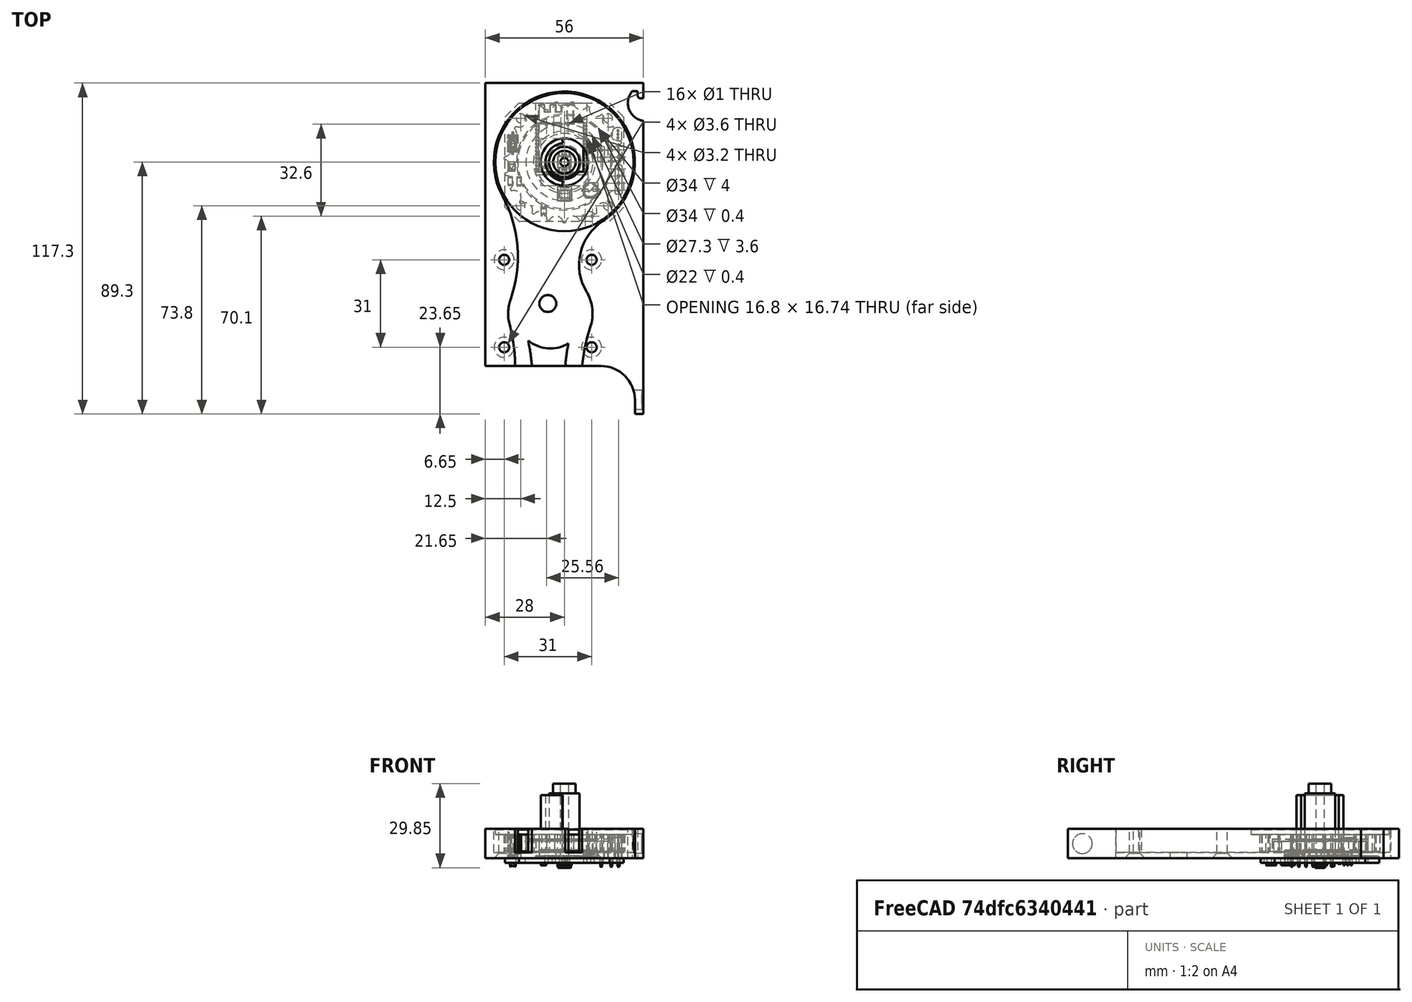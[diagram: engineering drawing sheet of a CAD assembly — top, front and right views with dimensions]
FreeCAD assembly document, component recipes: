
FREECAD ASSEMBLY — COMPONENT RECIPES ("integrated-roller-clutch-v2")

This assembly document has 6 components, labeled P0..P5 below (a component is one placed body or linked part). 5 of them carry a construction recipe — the FreeCAD feature program that regenerates the part from scratch, quoted from this document or its linked companion documents; the rest are supplied as boundary geometry only. No exploded tour is included for this assembly.
COMPONENT P0 — geometry summary ("driver-board"; no construction recipe available for this part):
  bounding box: 42.0 x 42.0 x 11.9 mm
  tessellated surface: 43,692 triangles
  volume: 4223 mm^3 (20% of its bounding box)
COMPONENT P1 — recipe-attached ("Bracket", modeled in this document).
Construction recipe (the document's own serialized feature program — sketch geometry with constraints, then the solid features built on it; lengths are millimeters unless a unit is written):

FEATURE [Sketcher::SketchObject] Sketch
  FullyConstrained = true
  MapMode = 5
  Support = -> [XY_Plane]
  expr: Constraints[10] = 50
  sketch-geometry (18):
    g0: Circle CenterX=0 CenterY=0 CenterZ=0 NormalX=0 NormalY=0 NormalZ=1 AngleXU=0 Radius=25
    g1: LineSegment StartX=-28 StartY=28 StartZ=0 EndX=28 EndY=28 EndZ=0
    g2: LineSegment StartX=28 StartY=28 StartZ=0 EndX=28 EndY=-89.3 EndZ=0
    g3: LineSegment StartX=28 StartY=-89.3 StartZ=0 EndX=25 EndY=-89.3 EndZ=0
    g4: LineSegment StartX=25 StartY=-89.3 StartZ=0 EndX=25 EndY=-84.3 EndZ=0
    g5: LineSegment StartX=13 StartY=-72.3 StartZ=0 EndX=-28 EndY=-72.3 EndZ=0
    g6: LineSegment StartX=-28 StartY=-72.3 StartZ=0 EndX=-28 EndY=28 EndZ=0
    g7: ArcOfCircle CenterX=13 CenterY=-84.3 CenterZ=0 NormalX=0 NormalY=0 NormalZ=1 AngleXU=0 Radius=12 StartAngle=0 EndAngle=1.5708
    g8: GeomPoint X=0 Y=-25 Z=0
    g9: GeomPoint X=0 Y=-30 Z=0
    g10: LineSegment StartX=14.3 StartY=-30 StartZ=0 EndX=-26 EndY=-30 EndZ=0
    g11: LineSegment StartX=-26 StartY=-30 StartZ=0 EndX=-26 EndY=-70.3 EndZ=0
    g12: LineSegment StartX=-26 StartY=-70.3 StartZ=0 EndX=14.3 EndY=-70.3 EndZ=0
    g13: LineSegment StartX=14.3 StartY=-70.3 StartZ=0 EndX=14.3 EndY=-30 EndZ=0
    g14: Circle CenterX=-5.85 CenterY=-50.15 CenterZ=0 NormalX=0 NormalY=0 NormalZ=1 AngleXU=0 Radius=28.4964
    g15: Circle CenterX=-5.85 CenterY=-50.15 CenterZ=0 NormalX=0 NormalY=0 NormalZ=1 AngleXU=0 Radius=3
    g16: LineSegment StartX=-28 StartY=-70.3 StartZ=0 EndX=-26 EndY=-70.3 EndZ=0
    g17: LineSegment StartX=-26 StartY=-70.3 StartZ=0 EndX=-26 EndY=-72.3 EndZ=0
  constraints (50):
    c: Coincident(g0,g-1)
    c: Horizontal(g1)
    c: Coincident(g2,g1)
    c: Vertical(g2)
    c: Coincident(g3,g2)
    c: Coincident(g4,g3)
    c: Horizontal(g5)
    c: Vertical(g6)
    c: Vertical(g4)
    c: Horizontal(g3)
    c: Diameter(g0) = 50
    c: Tangent(g7,g4) = -1.5708
    c: Distance(g3) = 3
    c: Tangent(g7,g5) = -1.5708
    c: Distance(g4) = 5
    c: PointOnObject(g8,g0)
    c: PointOnObject(g9,g-2)
    c: Distance(g9,g8) = 5
    c: Diameter(g7) = 24
    c: Coincident(g5,g6)
    c: Coincident(g10,g11)
    c: Coincident(g11,g12)
    c: Coincident(g12,g13)
    c: Coincident(g13,g10)
    c: Equal(g10,g11)
    c: Equal(g10,g12)
    c: Equal(g10,g13)
    c: PointOnObject(g10,g14)
    c: PointOnObject(g11,g14)
    c: PointOnObject(g12,g14)
    c: PointOnObject(g13,g14)
    c: Parallel(g12,g5)
    c: PointOnObject(g9,g10)
    c: Distance(g13) = 40.3
    c: Coincident(g15,g14)
    c: Diameter(g15) = 6
    c: Distance(g10) = 40.3
    c: PointOnObject(g16,g6)
    c: Coincident(g16,g11)
    c: Coincident(g17,g16)
    c: PointOnObject(g17,g5)
    c: Equal(g17,g16)
    c: Distance(g17) = 2
    c: Perpendicular(g12,g17)
    c: Perpendicular(g11,g16)
    c: PointOnObject(g8,g-2)
    c: DistanceY(g-1,g1) = 28
    c: DistanceX(g-1,g1) = 28
    c: Coincident(g1,g6)
    c: Distance(g1) = 56
FEATURE [PartDesign::Pad] Pad
  Direction = (0,0,1)
  Length = 10.4
  Length2 = 100
  Profile = -> Sketch
  Type = 0
  expr: Length = 2 mm + 0.2 mm + Pad001.Length + 0.2 mm + 2 mm
FEATURE [Sketcher::SketchObject] Sketch005
  ExternalGeometry = -> [Pad]
  FullyConstrained = true
  MapMode = 5
  Placement = pos=(0,0,0) rot=(1,0,0;3.14159rad)
  Support = -> [Pad]
  sketch-geometry (9):
    g0: LineSegment StartX=9.65 StartY=34.65 StartZ=0 EndX=9.65 EndY=65.65 EndZ=0
    g1: LineSegment StartX=9.65 StartY=65.65 StartZ=0 EndX=-21.35 EndY=65.65 EndZ=0
    g2: LineSegment StartX=-21.35 StartY=65.65 StartZ=0 EndX=-21.35 EndY=34.65 EndZ=0
    g3: LineSegment StartX=-21.35 StartY=34.65 StartZ=0 EndX=9.65 EndY=34.65 EndZ=0
    g4: Circle CenterX=-5.85 CenterY=50.15 CenterZ=0 NormalX=0 NormalY=0 NormalZ=1 AngleXU=0 Radius=21.9203
    g5: Circle CenterX=-21.35 CenterY=65.65 CenterZ=0 NormalX=0 NormalY=0 NormalZ=1 AngleXU=0 Radius=1.5
    g6: Circle CenterX=9.65 CenterY=65.65 CenterZ=0 NormalX=0 NormalY=0 NormalZ=1 AngleXU=0 Radius=1.5
    g7: Circle CenterX=9.65 CenterY=34.65 CenterZ=0 NormalX=0 NormalY=0 NormalZ=1 AngleXU=0 Radius=1.5
    g8: Circle CenterX=-21.35 CenterY=34.65 CenterZ=0 NormalX=0 NormalY=0 NormalZ=1 AngleXU=0 Radius=1.5
  constraints (22):
    c: Coincident(g0,g1)
    c: Coincident(g1,g2)
    c: Coincident(g2,g3)
    c: Coincident(g3,g0)
    c: Equal(g0,g1)
    c: Equal(g0,g2)
    c: Equal(g0,g3)
    c: PointOnObject(g0,g4)
    c: PointOnObject(g1,g4)
    c: PointOnObject(g2,g4)
    c: PointOnObject(g3,g4)
    c: Coincident(g4,g-4)
    c: Parallel(g1,g-3)
    c: Distance(g3) = 31
    c: Coincident(g5,g1)
    c: Coincident(g6,g0)
    c: Coincident(g7,g0)
    c: Coincident(g8,g2)
    c: Diameter(g8) = 3
    c: Equal(g8,g7)
    c: Equal(g8,g6)
    c: Equal(g8,g5)
FEATURE [PartDesign::Hole] Hole
  BaseFeature = -> Pad
  CustomThreadClearance = 0
  Depth = 25
  DepthType = 0
  Diameter = 3.6
  DrillForDepth = false
  DrillPoint = 1
  DrillPointAngle = 118
  HoleCutCountersinkAngle = 90
  HoleCutCustomValues = false
  HoleCutDepth = 0.5
  HoleCutDiameter = 7.1
  HoleCutType = 2
  ModelThread = false
  Profile = -> Sketch005
  Tapered = false
  TaperedAngle = 90
  ThreadClass = 0
  ThreadDepth = 23.5
  ThreadDepthType = 0
  ThreadDirection = 0
  ThreadFit = 2
  ThreadSize = 9
  ThreadType = 1
  Threaded = false
  UseCustomThreadClearance = false
FEATURE [Sketcher::SketchObject] Sketch006
  ExternalGeometry = -> [Hole]
  FullyConstrained = false
  MapMode = 5
  Placement = pos=(0,0,10.4) rot=(0,0,1;0rad)
  Support = -> [Hole]
  expr: Constraints[22] = 13 * 6 / pi
  expr: Constraints[23] = 13 * 6 / pi + 5.1
  expr: Constraints[7] = 50 mm
  sketch-geometry (13):
    g0: ArcOfCircle CenterX=0 CenterY=0 CenterZ=0 NormalX=0 NormalY=0 NormalZ=1 AngleXU=0 Radius=25 StartAngle=5.28927 EndAngle=9.92129
    g1: ArcOfCircle CenterX=-4.96805 CenterY=-53.6706 CenterZ=0 NormalX=0 NormalY=0 NormalZ=1 AngleXU=0 Radius=14.9641 StartAngle=2.8025 EndAngle=3.40354
    g2: ArcOfCircle CenterX=-4.96805 CenterY=-53.6706 CenterZ=0 NormalX=0 NormalY=0 NormalZ=1 AngleXU=0 Radius=14.9641 StartAngle=5.95611 EndAngle=6.82361
    g3: ArcOfCircle CenterX=-74.4541 CenterY=-72.3 CenterZ=0 NormalX=0 NormalY=0 NormalZ=1 AngleXU=0 Radius=56.9759 StartAngle=0 EndAngle=0.261943
    g4: ArcOfCircle CenterX=64.518 CenterY=-77.2446 CenterZ=0 NormalX=0 NormalY=0 NormalZ=1 AngleXU=0 Radius=58.412 StartAngle=2.81451 EndAngle=3.05684
    g5: ArcOfCircle CenterX=64.518 CenterY=-77.2446 CenterZ=0 NormalX=0 NormalY=0 NormalZ=1 AngleXU=0 Radius=64.3925 StartAngle=2.93924 EndAngle=3.06473
    g6: ArcOfCircle CenterX=-88.5335 CenterY=-79.2912 CenterZ=0 NormalX=0 NormalY=0 NormalZ=1 AngleXU=0 Radius=77.3718 StartAngle=0.0904824 EndAngle=0.208564
    g7: ArcOfCircle CenterX=-4.96805 CenterY=-53.6706 CenterZ=0 NormalX=0 NormalY=0 NormalZ=1 AngleXU=0 Radius=12.4141 StartAngle=4.0257 EndAngle=5.25473
    g8: ArcOfCircle CenterX=-61.9597 CenterY=-33.5686 CenterZ=0 NormalX=0 NormalY=0 NormalZ=1 AngleXU=0 Radius=45.4688 StartAngle=5.94409 EndAngle=6.7797
    g9: ArcOfCircle CenterX=23.7228 CenterY=-36.456 CenterZ=0 NormalX=0 NormalY=0 NormalZ=1 AngleXU=0 Radius=18.4949 StartAngle=2.14768 EndAngle=3.68201
    g10: LineSegment StartX=-17.4782 StartY=-72.3 StartZ=0 EndX=-11.4782 EndY=-72.3 EndZ=0
    g11: LineSegment StartX=0.315673 StartY=-72.3 StartZ=0 EndX=6.31567 EndY=-72.3 EndZ=0
    g12: GeomPoint X=-4.96805 Y=-74.7723 Z=0
  constraints (29):
    c: Coincident(g0,g-1)
    c: Coincident(g2,g1)
    c: Coincident(g5,g4)
    c: Coincident(g7,g1)
    c: Coincident(g7,g6)
    c: Coincident(g7,g5)
    c: Tangent(g9,g0) = 1.5708
    c: Diameter(g0) = 50
    c: Tangent(g0,g8) = 1.5708
    c: Tangent(g8,g1) = 1.5708
    c: Tangent(g2,g9) = 1.5708
    c: Equal(g2,g1)
    c: Tangent(g3,g1) = 1.5708
    c: Tangent(g2,g4) = 1.5708
    c: Coincident(g10,g3)
    c: Coincident(g10,g6)
    c: Coincident(g11,g5)
    c: Coincident(g11,g4)
    c: Equal(g10,g11)
    c: Distance(g10) = 6
    c: Vertical(g12,g1)
    c: Symmetric(g3,g4,g12)
    c: Diameter(g7) = 24.8282
    c: Diameter(g1) = 29.9282
    c: PointOnObject(g6,g-5)
    c: PointOnObject(g3,g-5)
    c: PointOnObject(g5,g-5)
    c: PointOnObject(g4,g-5)
    c: PointOnObject(g3,g-5)
FEATURE [PartDesign::Pocket] Pocket
  BaseFeature = -> Hole
  Direction = (0,0,-1)
  Length = 0
  Length2 = 100
  Offset = -2
  Profile = -> Sketch006
  Type = 3
  UpToFace = -> Hole [Face4]
FEATURE [Sketcher::SketchObject] Sketch007
  FullyConstrained = true
  MapMode = 5
  Placement = pos=(0,0,2) rot=(0,0,1;0rad)
  Support = -> [Pocket]
  expr: Constraints[1] = 33 mm
  expr: Constraints[3] = 22
  sketch-geometry (2):
    g0: Circle CenterX=0 CenterY=0 CenterZ=0 NormalX=0 NormalY=0 NormalZ=1 AngleXU=0 Radius=16.5
    g1: Circle CenterX=0 CenterY=0 CenterZ=0 NormalX=0 NormalY=0 NormalZ=1 AngleXU=0 Radius=11
  constraints (4):
    c: Coincident(g0,g-1)
    c: Diameter(g0) = 33
    c: Coincident(g1,g0)
    c: Diameter(g1) = 22
FEATURE [PartDesign::Pad] Pad002
  BaseFeature = -> Pocket
  Direction = (0,0,1)
  Length = 0.4
  Length2 = 100
  Profile = -> Sketch007
  Type = 0
FEATURE [Sketcher::SketchObject] Sketch020
  FullyConstrained = false
  MapMode = 5
  Placement = pos=(0,0,0) rot=(0.57735,0.57735,0.57735;2.0944rad)
  Support = -> [YZ_Plane]
  sketch-geometry (2):
    g0: Circle CenterX=-84.2293 CenterY=5.2 CenterZ=0 NormalX=0 NormalY=0 NormalZ=1 AngleXU=0 Radius=3.5
    g1: GeomPoint X=-80.7293 Y=5.2 Z=0
  constraints (3):
    c: Diameter(g0) = 7
    c: PointOnObject(g1,g0)
    c: Horizontal(g1,g0)
FEATURE [Sketcher::SketchObject] Sketch019
  FullyConstrained = false
  MapMode = 5
  Placement = pos=(0,0,10.4) rot=(0,0,1;0rad)
  sketch-geometry (7):
    g0: LineSegment StartX=28.0692 StartY=22.5865 StartZ=0 EndX=27.0025 EndY=22.5865 EndZ=0
    g1: LineSegment StartX=26.0025 StartY=23.5865 StartZ=0 EndX=26.0025 EndY=25.0865 EndZ=0
    g2: LineSegment StartX=26.0025 StartY=25.0865 StartZ=0 EndX=24.0025 EndY=25.0865 EndZ=0
    g3: ArcOfCircle CenterX=28.9326 CenterY=20.9584 CenterZ=0 NormalX=0 NormalY=0 NormalZ=1 AngleXU=0 Radius=6.43014 StartAngle=2.4445 EndAngle=4.57772
    g4: LineSegment StartX=28.0692 StartY=14.5865 StartZ=0 EndX=28.0692 EndY=22.5865 EndZ=0
    g5: ArcOfCircle CenterX=27.0025 CenterY=23.5865 CenterZ=0 NormalX=0 NormalY=0 NormalZ=1 AngleXU=0 Radius=1 StartAngle=3.14159 EndAngle=4.71239
    g6: GeomPoint X=22.5025 Y=20.9865 Z=0
  constraints (16):
    c: Horizontal(g0)
    c: Vertical(g1)
    c: Coincident(g2,g1)
    c: Horizontal(g2)
    c: Coincident(g3,g2)
    c: Coincident(g4,g3)
    c: Coincident(g4,g0)
    c: Tangent(g1,g5) = 1.5708
    c: Tangent(g0,g5) = 1.5708
    c: Distance(g4) = 8
    c: DistanceY(g0,g1) = 2.5
    c: PointOnObject(g6,g3)
    c: DistanceY(g6,g2) = 4.1
    c: Radius(g5) = 1
    c: Distance(g2) = 2
    c: DistanceX(g6,g1) = 3.5
FEATURE [Sketcher::SketchObject] Sketch021
  ExternalGeometry = -> [Pad002]
  FullyConstrained = true
  MapMode = 5
  Placement = pos=(0,0,2.4) rot=(0,0,1;0rad)
  Support = -> [Pad002]
  expr: Constraints[1] = 27.3
  sketch-geometry (2):
    g0: Circle CenterX=0 CenterY=0 CenterZ=0 NormalX=0 NormalY=0 NormalZ=1 AngleXU=0 Radius=13.65
    g1: Circle CenterX=0 CenterY=0 CenterZ=0 NormalX=0 NormalY=0 NormalZ=1 AngleXU=0 Radius=16.5
  constraints (4):
    c: Coincident(g0,g-1)
    c: Diameter(g0) = 27.3
    c: Coincident(g1,g0)
    c: Equal(g1,g-3)
FEATURE [PartDesign::Pad] Pad023
  BaseFeature = -> Pad002
  Direction = (0,0,1)
  Length = 3.6
  Length2 = 100
  Profile = -> Sketch021
  Type = 0
FEATURE [Sketcher::SketchObject] Sketch023
  FullyConstrained = true
  MapMode = 5
  Placement = pos=(0,0,2) rot=(0,0,1;0rad)
  Support = -> [Pad023]
  sketch-geometry (1):
    g0: Circle CenterX=0 CenterY=0 CenterZ=0 NormalX=0 NormalY=0 NormalZ=1 AngleXU=0 Radius=6
  constraints (2):
    c: Coincident(g0,g-1)
    c: Diameter(g0) = 12
FEATURE [PartDesign::Pad] Pad024
  BaseFeature = -> Pad023
  Direction = (0,0,1)
  Length = 1
  Length2 = 100
  Profile = -> Sketch023
  Type = 0
FEATURE [Sketcher::SketchObject] Sketch024
  FullyConstrained = true
  MapMode = 5
  Placement = pos=(0,0,3) rot=(0,0,1;0rad)
  Support = -> [Pad024]
  sketch-geometry (1):
    g0: Circle CenterX=0 CenterY=0 CenterZ=0 NormalX=0 NormalY=0 NormalZ=1 AngleXU=0 Radius=5.4
  constraints (2):
    c: Coincident(g0,g-1)
    c: Diameter(g0) = 10.8
FEATURE [PartDesign::Pad] Pad025
  BaseFeature = -> Pad024
  Direction = (0,0,1)
  Length = 20
  Length2 = 100
  Profile = -> Sketch024
  Type = 0
FEATURE [Sketcher::SketchObject] Sketch054
  FullyConstrained = true
  MapMode = 5
  Placement = pos=(0,0,23) rot=(0,0,1;0rad)
  Support = -> [Pad025]
  sketch-geometry (1):
    g0: Circle CenterX=0 CenterY=0 CenterZ=0 NormalX=0 NormalY=0 NormalZ=1 AngleXU=0 Radius=4
  constraints (2):
    c: Coincident(g0,g-1)
    c: Diameter(g0) = 8
FEATURE [PartDesign::Pad] Pad026
  BaseFeature = -> Pad025
  Direction = (0,0,1)
  Length = 3.5
  Length2 = 100
  Profile = -> Sketch054
  Type = 0
FEATURE [PartDesign::Pocket] Pocket007
  BaseFeature = -> Pad026
  Direction = (0,0,-1)
  Length = 5
  Length2 = 100
  Profile = -> Sketch019
  Type = 1
FEATURE [PartDesign::Pocket] Pocket008
  BaseFeature = -> Pocket007
  Direction = (-1,2e-16,-3e-16)
  Length = 0
  Length2 = 100
  Offset = -1.5
  Profile = -> Sketch020
  Type = 3
  UpToFace = -> Pocket007 [Face9]
FEATURE [PartDesign::Hole] Hole001
  BaseFeature = -> Pocket008
  CustomThreadClearance = 0
  Depth = 25
  DepthType = 0
  Diameter = 3.4
  DrillForDepth = false
  DrillPoint = 1
  DrillPointAngle = 118
  HoleCutCountersinkAngle = 90
  HoleCutCustomValues = false
  HoleCutDepth = 0
  HoleCutDiameter = 6.1
  HoleCutType = 0
  ModelThread = false
  Profile = -> Pocket008 [Edge105]
  Tapered = false
  TaperedAngle = 90
  ThreadClass = 0
  ThreadDepth = 23.5
  ThreadDepthType = 0
  ThreadDirection = 0
  ThreadFit = 0
  ThreadSize = 9
  ThreadType = 1
  Threaded = false
  UseCustomThreadClearance = false
FEATURE [PartDesign::Hole] Hole003
  BaseFeature = -> Hole001
  CustomThreadClearance = 0
  Depth = 267.965
  DepthType = 1
  Diameter = 2.9
  DrillForDepth = false
  DrillPoint = 1
  DrillPointAngle = 118
  HoleCutCountersinkAngle = 90
  HoleCutCustomValues = false
  HoleCutDepth = 0
  HoleCutDiameter = 6.1
  HoleCutType = 0
  ModelThread = false
  Profile = -> Pad026 [Face43]
  Tapered = false
  TaperedAngle = 90
  ThreadClass = 0
  ThreadDepth = 267.965
  ThreadDepthType = 0
  ThreadDirection = 0
  ThreadFit = 0
  ThreadSize = 0
  ThreadType = 0
  Threaded = false
  UseCustomThreadClearance = false
FEATURE [PartDesign::Body] Body  label="Bracket"
  Group = -> [Sketch,Pad,Sketch005,Hole,Sketch006,Pocket,Sketch007,Pad002,Pad023,Pad024,Pad025,Pad026,Sketch054,Sketch021,Sketch023,Sketch024,Sketch019,Pocket007,Sketch020,Pocket008,Hole001,Hole003]
  Origin = -> Origin
  Tip = -> Hole003
COMPONENT P2 — recipe-attached ("Stepper Gear", modeled in this document).
Construction recipe (the document's own serialized feature program — sketch geometry with constraints, then the solid features built on it; lengths are millimeters unless a unit is written):

FEATURE [Sketcher::SketchObject] Sketch003
  FullyConstrained = true
  MapMode = 5
  Support = -> [XY_Plane001]
  expr: Constraints[7] = 13 * 6 / pi - 1
  sketch-geometry (3):
    g0: Circle CenterX=0 CenterY=0 CenterZ=0 NormalX=0 NormalY=0 NormalZ=1 AngleXU=0 Radius=11.9141
    g1: ArcOfCircle CenterX=0 CenterY=0 CenterZ=0 NormalX=0 NormalY=0 NormalZ=1 AngleXU=0 Radius=2.575 StartAngle=2.28245 EndAngle=7.14233
    g2: LineSegment StartX=-1.6817 StartY=1.95 StartZ=0 EndX=1.6817 EndY=1.95 EndZ=0
  constraints (8):
    c: Coincident(g0,g-1)
    c: Coincident(g1,g0)
    c: Coincident(g2,g1)
    c: Coincident(g2,g1)
    c: Horizontal(g2)
    c: Diameter(g1) = 5.15
    c: Distance(g0,g2) = 1.95
    c: Diameter(g0) = 23.8282
FEATURE [PartDesign::Pad] Pad001
  Direction = (1,1,1)
  Length = 6
  Length2 = 100
  Profile = -> Sketch003
  Type = 0
FEATURE [Sketcher::SketchObject] Sketch004
  ExternalGeometry = -> [Pad001]
  FullyConstrained = true
  MapMode = 5
  Placement = pos=(0,0,6) rot=(0,0,1;0rad)
  Support = -> [Pad001]
  sketch-geometry (2):
    g0: Circle CenterX=0 CenterY=12.4141 CenterZ=0 NormalX=0 NormalY=0 NormalZ=1 AngleXU=0 Radius=2.55
    g1: GeomPoint X=0 Y=11.9141 Z=0
  constraints (6):
    c: PointOnObject(g0,g-2)
    c: PointOnObject(g1,g-2)
    c: PointOnObject(g1,g-3)
    c: Distance(g0,g1) = 0.5
    c: Diameter(g0) = 5.1
    c: Distance(g-1,g0) = 12.4141
FEATURE [PartDesign::Pocket] Pocket001
  BaseFeature = -> Pad001
  Direction = (1,1,1)
  Length = 5
  Length2 = 100
  Profile = -> Sketch004
  Type = 1
FEATURE [PartDesign::PolarPattern] PolarPattern
  Angle = 360
  Axis = -> Sketch004 [N_Axis]
  BaseFeature = -> Pocket001
  Occurrences = 13
  Originals = -> [Pocket001]
FEATURE [Sketcher::SketchObject] Sketch062
  ExternalGeometry = -> [PolarPattern]
  FullyConstrained = true
  MapMode = 5
  Placement = pos=(0,0,6) rot=(0,0,1;0rad)
  Support = -> [PolarPattern]
  sketch-geometry (1):
    g0: Circle CenterX=0 CenterY=0 CenterZ=0 NormalX=0 NormalY=0 NormalZ=1 AngleXU=0 Radius=2.575
  constraints (2):
    c: Coincident(g0,g-1)
    c: Tangent(g0,g-3)
FEATURE [PartDesign::Pocket] Pocket014
  BaseFeature = -> PolarPattern
  Direction = (1,1,1)
  Length = 1.2
  Length2 = 100
  Profile = -> Sketch062
  Type = 0
FEATURE [PartDesign::Body] Body001  label="Stepper Gear"
  Group = -> [Sketch003,Pad001,Sketch004,Pocket001,PolarPattern,Sketch062,Pocket014]
  Origin = -> Origin001
  Placement = pos=(-5.85,-50.15,2.4) rot=(0,0,1;1.5708rad)
  Tip = -> Pocket014
  expr: .Placement.Base.x = -28 + 2 + 40.3 / 2
  expr: .Placement.Base.y = -(25 + 5 + 40.3 / 2)
  expr: .Placement.Base.z = 2 + 0.4
COMPONENT P3 — recipe-attached ("Cover Gear", modeled in this document).
Construction recipe (the document's own serialized feature program — sketch geometry with constraints, then the solid features built on it; lengths are millimeters unless a unit is written):

FEATURE [Sketcher::SketchObject] Sketch012
  FullyConstrained = true
  MapMode = 5
  Support = -> [XY_Plane002]
  expr: Constraints[1] = 23 * 5.85 / pi
  sketch-geometry (1):
    g0: Circle CenterX=0 CenterY=0 CenterZ=0 NormalX=0 NormalY=0 NormalZ=1 AngleXU=0 Radius=21.4143
  constraints (2):
    c: Coincident(g0,g-1)
    c: Diameter(g0) = 42.8286
FEATURE [PartDesign::Pad] Pad007
  Direction = (1,1,1)
  Length = 6
  Length2 = 100
  Profile = -> Sketch012
  Type = 0
  expr: Length = Pad001.Length
FEATURE [Sketcher::SketchObject] Sketch013
  ExternalGeometry = -> [Pad007]
  FullyConstrained = true
  MapMode = 5
  Placement = pos=(0,0,6) rot=(0,0,1;0rad)
  Support = -> [Pad007]
  sketch-geometry (2):
    g0: Circle CenterX=0 CenterY=21.9143 CenterZ=0 NormalX=0 NormalY=0 NormalZ=1 AngleXU=0 Radius=2.55
    g1: GeomPoint X=0 Y=21.4143 Z=0
  constraints (5):
    c: PointOnObject(g0,g-2)
    c: PointOnObject(g1,g-3)
    c: PointOnObject(g1,g-2)
    c: Distance(g1,g0) = 0.5
    c: Diameter(g0) = 5.1
FEATURE [PartDesign::Pocket] Pocket002
  BaseFeature = -> Pad007
  Direction = (1,1,1)
  Length = 5
  Length2 = 100
  Profile = -> Sketch013
  Type = 1
FEATURE [PartDesign::PolarPattern] PolarPattern001
  Angle = 360
  Axis = -> Sketch013 [N_Axis]
  BaseFeature = -> Pocket002
  Occurrences = 23
  Originals = -> [Pocket002]
FEATURE [Sketcher::SketchObject] Sketch014
  FullyConstrained = true
  MapMode = 5
  Placement = pos=(0,0,0) rot=(1,0,0;3.14159rad)
  Support = -> [PolarPattern001]
  expr: Constraints[1] = 27 + 6 + 1
  expr: Constraints[3] = 20.3
  sketch-geometry (2):
    g0: Circle CenterX=0 CenterY=0 CenterZ=0 NormalX=0 NormalY=0 NormalZ=1 AngleXU=0 Radius=17
    g1: Circle CenterX=0 CenterY=0 CenterZ=0 NormalX=0 NormalY=0 NormalZ=1 AngleXU=0 Radius=10.15
  constraints (4):
    c: Coincident(g0,g-1)
    c: Diameter(g0) = 34
    c: Coincident(g1,g0)
    c: Diameter(g1) = 20.3
FEATURE [PartDesign::Pocket] Pocket003
  BaseFeature = -> PolarPattern001
  Direction = (0,0,1)
  Length = 4
  Length2 = 100
  Profile = -> Sketch014
  Type = 0
FEATURE [Sketcher::SketchObject] Sketch015
  FullyConstrained = true
  MapMode = 5
  Placement = pos=(0,0,0) rot=(1,0,0;3.14159rad)
  Support = -> [Pocket003]
  expr: Constraints[1] = 16.8
  sketch-geometry (1):
    g0: Circle CenterX=0 CenterY=0 CenterZ=0 NormalX=0 NormalY=0 NormalZ=1 AngleXU=0 Radius=8.4
  constraints (2):
    c: Coincident(g0,g-1)
    c: Diameter(g0) = 16.8
FEATURE [PartDesign::Pocket] Pocket004
  BaseFeature = -> Pocket003
  Direction = (0,0,1)
  Length = 5
  Length2 = 100
  Profile = -> Sketch015
  Type = 1
FEATURE [Sketcher::SketchObject] Sketch016
  ExternalGeometry = -> [Pocket004]
  FullyConstrained = true
  MapMode = 5
  Placement = pos=(0,0,0) rot=(1,0,0;3.14159rad)
  Support = -> [Pocket004]
  sketch-geometry (6):
    g0: ArcOfCircle CenterX=0 CenterY=0 CenterZ=0 NormalX=0 NormalY=0 NormalZ=1 AngleXU=0 Radius=8.4 StartAngle=1.65806 EndAngle=4.62512
    g1: ArcOfCircle CenterX=0 CenterY=0 CenterZ=0 NormalX=0 NormalY=0 NormalZ=1 AngleXU=0 Radius=6.7 StartAngle=1.65806 EndAngle=4.62512
    g2: LineSegment StartX=-0.732108 StartY=8.36804 StartZ=0 EndX=-0.583943 EndY=6.6745 EndZ=0
    g3: LineSegment StartX=-0.732108 StartY=-8.36804 StartZ=0 EndX=-0.583943 EndY=-6.6745 EndZ=0
    g4: LineSegment StartX=-0.583943 StartY=-6.6745 StartZ=0 EndX=8.4 EndY=0 EndZ=0
    g5: LineSegment StartX=8.4 StartY=0 StartZ=0 EndX=-0.583943 EndY=6.6745 EndZ=0
  constraints (17):
    c: Coincident(g0,g-1)
    c: PointOnObject(g0,g-3)
    c: Coincident(g1,g0)
    c: Coincident(g2,g0)
    c: Coincident(g2,g1)
    c: Coincident(g3,g0)
    c: Coincident(g3,g1)
    c: Perpendicular(g0,g3)
    c: Perpendicular(g0,g2)
    c: Diameter(g1) = 13.4
    c: Angle(g2,g3) = 2.96706
    c: Coincident(g4,g1)
    c: PointOnObject(g4,g-1)
    c: Coincident(g5,g4)
    c: Coincident(g5,g1)
    c: Equal(g4,g5)
    c: PointOnObject(g4,g-3)
FEATURE [PartDesign::Pad] Pad008
  BaseFeature = -> Pocket004
  Direction = (0,0,-1)
  Length = 20
  Length2 = 100
  Profile = -> Sketch016
  Reversed = true
  Type = 0
FEATURE [Sketcher::SketchObject] Sketch018
  ExternalGeometry = -> [Pad008]
  FullyConstrained = true
  MapMode = 5
  Placement = pos=(0,0,6) rot=(0,0,1;0rad)
  Support = -> [Pad008]
  sketch-geometry (2):
    g0: Circle CenterX=0 CenterY=0 CenterZ=0 NormalX=0 NormalY=0 NormalZ=1 AngleXU=0 Radius=24.5
    g1: Circle CenterX=0 CenterY=0 CenterZ=0 NormalX=0 NormalY=0 NormalZ=1 AngleXU=0 Radius=8.4
  constraints (4):
    c: Coincident(g0,g-1)
    c: Coincident(g1,g0)
    c: PointOnObject(g-3,g1)
    c: Diameter(g0) = 49
FEATURE [PartDesign::Pad] Pad009
  BaseFeature = -> Pad008
  Direction = (0,0,1)
  Length = 1.8
  Length2 = 100
  Profile = -> Sketch018
  Type = 0
FEATURE [Sketcher::SketchObject] Sketch060
  ExternalGeometry = -> [Pad009]
  FullyConstrained = true
  MapMode = 5
  Placement = pos=(0,0,4) rot=(1,0,0;3.14159rad)
  Support = -> [Pad009]
  sketch-geometry (2):
    g0: Circle CenterX=0 CenterY=0 CenterZ=0 NormalX=0 NormalY=0 NormalZ=1 AngleXU=0 Radius=17
    g1: Circle CenterX=0 CenterY=0 CenterZ=0 NormalX=0 NormalY=0 NormalZ=1 AngleXU=0 Radius=11
  constraints (4):
    c: Coincident(g0,g-1)
    c: Equal(g0,g-3)
    c: Coincident(g1,g0)
    c: Diameter(g1) = 22
FEATURE [PartDesign::Pocket] Pocket013
  BaseFeature = -> Pad009
  Direction = (0,0,1)
  Length = 0.4
  Length2 = 100
  Profile = -> Sketch060
  Type = 0
FEATURE [PartDesign::Body] Body002  label="Cover Gear"
  Group = -> [Sketch012,Pad007,Sketch013,Pocket002,PolarPattern001,Sketch014,Pocket003,Sketch015,Pocket004,Sketch016,Pad008,Sketch018,Pad009,Sketch060,Pocket013]
  Origin = -> Origin002
  Placement = pos=(0,0,2.4) rot=(0,0,1;0rad)
  Tip = -> Pocket013
  expr: .Placement.Base.z = 2 + 0.4
COMPONENT P4 — recipe-attached ("Spring", modeled in this document).
Construction recipe (the document's own serialized feature program — sketch geometry with constraints, then the solid features built on it; lengths are millimeters unless a unit is written):

FEATURE [Sketcher::SketchObject] Sketch017
  FullyConstrained = true
  MapMode = 5
  Placement = pos=(0,0,0) rot=(1,0,0;1.5708rad)
  Support = -> [XZ_Plane003]
  expr: Constraints[9] = 10.5 / 2
  sketch-geometry (4):
    g0: LineSegment StartX=5.25 StartY=0 StartZ=0 EndX=6.1 EndY=0 EndZ=0
    g1: LineSegment StartX=6.1 StartY=0 StartZ=0 EndX=6.1 EndY=1.25 EndZ=0
    g2: LineSegment StartX=6.1 StartY=1.25 StartZ=0 EndX=5.25 EndY=1.25 EndZ=0
    g3: LineSegment StartX=5.25 StartY=1.25 StartZ=0 EndX=5.25 EndY=0 EndZ=0
  constraints (12):
    c: Coincident(g0,g1)
    c: Coincident(g1,g2)
    c: Coincident(g2,g3)
    c: Coincident(g3,g0)
    c: Horizontal(g0)
    c: Horizontal(g2)
    c: Vertical(g1)
    c: Vertical(g3)
    c: PointOnObject(g0,g-1)
    c: Distance(g-1,g0) = 5.25
    c: Distance(g1) = 1.25
    c: Distance(g0) = 0.85
FEATURE [PartDesign::AdditiveHelix] AdditiveHelix
  Angle = 0
  Axis = (0,-2e-16,1)
  Base = (0,0,0)
  Growth = 0
  HasBeenEdited = true
  Height = 8.1
  LeftHanded = false
  Mode = 2
  Outside = false
  Pitch = 1.24615
  Placement = pos=(0,0,0) rot=(1,0,0;1.5708rad)
  Profile = -> Sketch017
  ReferenceAxis = -> Sketch017 [V_Axis]
  Turns = 6.5
FEATURE [PartDesign::Body] Body003  label="Spring"
  Group = -> [Sketch017,AdditiveHelix]
  Origin = -> Origin003
  Placement = pos=(0,0,2.2) rot=(0,0,1;0rad)
  Tip = -> AdditiveHelix
COMPONENT P5 — recipe-attached ("Cover Adapter", modeled in this document).
Construction recipe (the document's own serialized feature program — sketch geometry with constraints, then the solid features built on it; lengths are millimeters unless a unit is written):

FEATURE [Sketcher::SketchObject] Sketch049
  FullyConstrained = true
  MapMode = 5
  Support = -> [XY_Plane011]
  sketch-geometry (7):
    g0: ArcOfCircle CenterX=0 CenterY=0 CenterZ=0 NormalX=0 NormalY=0 NormalZ=1 AngleXU=0 Radius=8.1 StartAngle=4.99164 EndAngle=7.57473
    g1: ArcOfCircle CenterX=0 CenterY=0 CenterZ=0 NormalX=0 NormalY=0 NormalZ=1 AngleXU=0 Radius=6.5 StartAngle=4.99164 EndAngle=7.57473
    g2: LineSegment StartX=1.79164 StartY=6.2482 StartZ=0 EndX=2.23266 EndY=7.78622 EndZ=0
    g3: LineSegment StartX=1.79164 StartY=-6.2482 StartZ=0 EndX=2.23266 EndY=-7.78622 EndZ=0
    g4: GeomPoint X=-5 Y=0 Z=0
    g5: LineSegment StartX=-5 StartY=0 StartZ=0 EndX=1.79164 EndY=6.2482 EndZ=0
    g6: LineSegment StartX=-5 StartY=0 StartZ=0 EndX=1.79164 EndY=-6.2482 EndZ=0
  constraints (18):
    c: Coincident(g0,g-1)
    c: Coincident(g1,g0)
    c: Coincident(g2,g1)
    c: Coincident(g2,g0)
    c: Coincident(g3,g1)
    c: Coincident(g3,g0)
    c: Perpendicular(g0,g2)
    c: Perpendicular(g1,g3)
    c: Diameter(g1) = 13
    c: Angle(g3,g2) = 2.58309
    c: PointOnObject(g4,g-1)
    c: Coincident(g5,g4)
    c: Coincident(g5,g1)
    c: Coincident(g6,g4)
    c: Coincident(g6,g1)
    c: Equal(g6,g5)
    c: Distance(g4,g0) = 5
    c: Distance(g2) = 1.6
FEATURE [Sketcher::SketchObject] Sketch050
  FullyConstrained = true
  MapMode = 5
  Placement = pos=(0,0,8.4) rot=(0,0,1;0rad)
  sketch-geometry (1):
    g0: Circle CenterX=0 CenterY=0 CenterZ=0 NormalX=0 NormalY=0 NormalZ=1 AngleXU=0 Radius=12.4
  constraints (2):
    c: Coincident(g0,g-1)
    c: Diameter(g0) = 24.8
FEATURE [PartDesign::Pad] Pad022
  AllowMultiFace = false
  Direction = (1,1,1)
  Length = 20
  Length2 = 100
  Placement = pos=(0,0,8.4) rot=(0,0,1;0rad)
  Profile = -> Sketch050
  Type = 0
  expr: Length = 20
FEATURE [Sketcher::SketchObject] Sketch058
  FullyConstrained = true
  MapMode = 5
  Placement = pos=(0,0,24.1) rot=(1,0,0;3.14159rad)
  sketch-geometry (1):
    g0: Circle CenterX=0 CenterY=0 CenterZ=0 NormalX=0 NormalY=0 NormalZ=1 AngleXU=0 Radius=5.5
  constraints (2):
    c: Coincident(g0,g-1)
    c: Diameter(g0) = 11
FEATURE [PartDesign::Pad] Pad027
  BaseFeature = -> Pad022
  Direction = (1,1,1)
  Length = 10
  Length2 = 100
  Placement = pos=(0,0,8.4) rot=(0,0,1;0rad)
  Profile = -> Sketch049
  Type = 3
  UpToFace = -> Pad022 [Face2]
FEATURE [Sketcher::SketchObject] Sketch056
  ExternalGeometry = -> [Pad027]
  FullyConstrained = true
  MapMode = 5
  Placement = pos=(0,0,8.4) rot=(1,0,0;3.14159rad)
  sketch-geometry (4):
    g0: ArcOfCircle CenterX=0 CenterY=0 CenterZ=0 NormalX=0 NormalY=0 NormalZ=1 AngleXU=0 Radius=9 StartAngle=1.29154 EndAngle=4.99164
    g1: ArcOfCircle CenterX=0 CenterY=0 CenterZ=0 NormalX=0 NormalY=0 NormalZ=1 AngleXU=0 Radius=6.5 StartAngle=4.99164 EndAngle=7.57473
    g2: LineSegment StartX=1.79164 StartY=6.2482 StartZ=0 EndX=2.48074 EndY=8.65136 EndZ=0
    g3: LineSegment StartX=1.79164 StartY=-6.2482 StartZ=0 EndX=2.48074 EndY=-8.65136 EndZ=0
  constraints (11):
    c: Coincident(g0,g-1)
    c: Coincident(g1,g0)
    c: Coincident(g1,g-3)
    c: Coincident(g1,g-3)
    c: Coincident(g2,g1)
    c: Coincident(g3,g1)
    c: Coincident(g0,g2)
    c: Coincident(g0,g3)
    c: PointOnObject(g-4,g2)
    c: PointOnObject(g-4,g3)
    c: Diameter(g0) = 18
FEATURE [PartDesign::Pocket] Pocket009
  BaseFeature = -> Pad027
  Direction = (1,1,1)
  Length = 12.2
  Length2 = 100
  Placement = pos=(0,0,8.4) rot=(0,0,1;0rad)
  Profile = -> Sketch056
  Type = 0
FEATURE [Sketcher::SketchObject] Sketch057
  FullyConstrained = true
  MapMode = 5
  Placement = pos=(0,0,20.6) rot=(1,0,0;3.14159rad)
  Support = -> [Pocket009]
  sketch-geometry (1):
    g0: Circle CenterX=0 CenterY=0 CenterZ=0 NormalX=0 NormalY=0 NormalZ=1 AngleXU=0 Radius=6.05
  constraints (2):
    c: Coincident(g0,g-1)
    c: Diameter(g0) = 12.1
FEATURE [PartDesign::Pocket] Pocket010
  BaseFeature = -> Pocket009
  Direction = (1,1,1)
  Length = 3.5
  Length2 = 100
  Placement = pos=(0,0,8.4) rot=(0,0,1;0rad)
  Profile = -> Sketch057
  Type = 0
FEATURE [PartDesign::Pocket] Pocket011
  BaseFeature = -> Pocket010
  Direction = (1,1,1)
  Length = 5
  Length2 = 100
  Placement = pos=(0,0,8.4) rot=(0,0,1;0rad)
  Profile = -> Sketch058
  Type = 1
FEATURE [Sketcher::SketchObject] Sketch055
  ExternalGeometry = -> [Pocket011]
  FullyConstrained = true
  MapMode = 5
  Placement = pos=(0,0,28.4) rot=(0,0,1;0rad)
  Support = -> [Pocket011]
  sketch-geometry (4):
    g0: ArcOfCircle CenterX=0 CenterY=0 CenterZ=0 NormalX=0 NormalY=0 NormalZ=1 AngleXU=0 Radius=12.4 StartAngle=5.71595 EndAngle=6.85042
    g1: ArcOfCircle CenterX=0 CenterY=0 CenterZ=0 NormalX=0 NormalY=0 NormalZ=1 AngleXU=0 Radius=8.1 StartAngle=5.71595 EndAngle=6.85042
    g2: LineSegment StartX=6.83147 StartY=-4.35213 StartZ=0 EndX=10.4581 EndY=-6.66252 EndZ=0
    g3: LineSegment StartX=6.83147 StartY=4.35213 StartZ=0 EndX=10.4581 EndY=6.66252 EndZ=0
  constraints (12):
    c: Coincident(g0,g-1)
    c: Coincident(g1,g0)
    c: Coincident(g2,g1)
    c: Coincident(g2,g0)
    c: Coincident(g3,g1)
    c: Coincident(g3,g0)
    c: PointOnObject(g0,g3)
    c: PointOnObject(g0,g2)
    c: Diameter(g0) = 24.8
    c: Symmetric(g1,g1,g-1)
    c: Angle(g2,g3) = 1.13446
    c: Equal(g-3,g1)
FEATURE [PartDesign::Pocket] Pocket012
  BaseFeature = -> Pocket011
  Direction = (1,1,1)
  Length = 5
  Length2 = 100
  Placement = pos=(0,0,8.4) rot=(0,0,1;0rad)
  Profile = -> Sketch055
  Type = 1
FEATURE [Sketcher::SketchObject] Sketch059
  ExternalGeometry = -> [Pocket012]
  FullyConstrained = true
  MapMode = 5
  Placement = pos=(-7e-16,1.1e-15,8.4) rot=(0.924535,0.269477,0.269477;1.64918rad)
  Support = -> [Pocket012]
  sketch-geometry (3):
    g0: LineSegment StartX=12.4 StartY=0 StartZ=0 EndX=13.9 EndY=0 EndZ=0
    g1: LineSegment StartX=12.4 StartY=3.5707 StartZ=0 EndX=12.4 EndY=0 EndZ=0
    g2: ArcOfCircle CenterX=17.4 CenterY=3.57071 CenterZ=0 NormalX=0 NormalY=0 NormalZ=1 AngleXU=0 Radius=5 StartAngle=3.1416 EndAngle=3.93699
  constraints (9):
    c: Coincident(g0,g-3)
    c: PointOnObject(g0,g-1)
    c: PointOnObject(g1,g-3)
    c: Coincident(g1,g0)
    c: Distance(g0) = 1.5
    c: Coincident(g2,g1)
    c: Tangent(g2,g-3)
    c: Coincident(g2,g0)
    c: Diameter(g2) = 10
FEATURE [PartDesign::Revolution] Revolution
  Angle = 295
  Axis = (1e-16,-3e-16,1)
  Base = (-7e-16,1.1e-15,8.4)
  BaseFeature = -> Pocket012
  Placement = pos=(0,0,8.4) rot=(0,0,1;0rad)
  Profile = -> Sketch059
  ReferenceAxis = -> Sketch059 [V_Axis]
  expr: Angle = 360 - 65
FEATURE [PartDesign::Body] Body006  label="Cover Adapter"
  Group = -> [Sketch050,Pad022,Sketch056,Sketch049,Pad027,Pocket009,Sketch057,Pocket010,Sketch058,Pocket011,Sketch055,Pocket012,Sketch059,Revolution]
  Origin = -> Origin011
  Placement = pos=(0,0,2.4) rot=(0,0,1;0rad)
  Tip = -> Revolution
PROVENANCE & LICENSES
A FreeCAD (.FCStd) document from a public repository crawl; recipes are the document's own serialized feature recipes (and, for linked parts, companion documents' recipes).
License: as declared in the source repository (recorded in the dataset sidecar).
